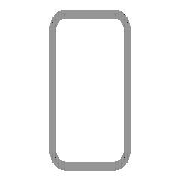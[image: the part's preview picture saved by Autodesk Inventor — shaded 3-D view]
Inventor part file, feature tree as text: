
AUTODESK INVENTOR PART (.ipt)
format: ipt  version: 2025 (Build 290162010, 162A)  size: 135,168 bytes
history: native  units: mm (DEFAULTED — no unit token found)
features: other x4, sketch x1, plane x1
ambient origin geometry x8: Origin, YZ Plane, XZ Plane, XY Plane, X Axis, Y Axis, Z Axis, Center Point
bodies: Solid1 (feature_tree), Body (feature_tree)
feature tree (6):
  parser-record x1  (decoder bookkeeping rows leaked as tree rows — omitted from the tree; the rows remain in map.json)
  other  "Driven Length"
  other  "Start Plane"
  other  "End Plane"
  sketch  "Sketch3"  dims[d3=2200.0mm d4=0.0mm d7=6.0mm d9=40.0mm d11=80.0mm d12=3.0mm d13=-0.0mm d14=2200.0mm d15=20.0mm d16=40.0mm d17=90.0deg d18=2200.0mm]
  plane  "Work Plane3"
